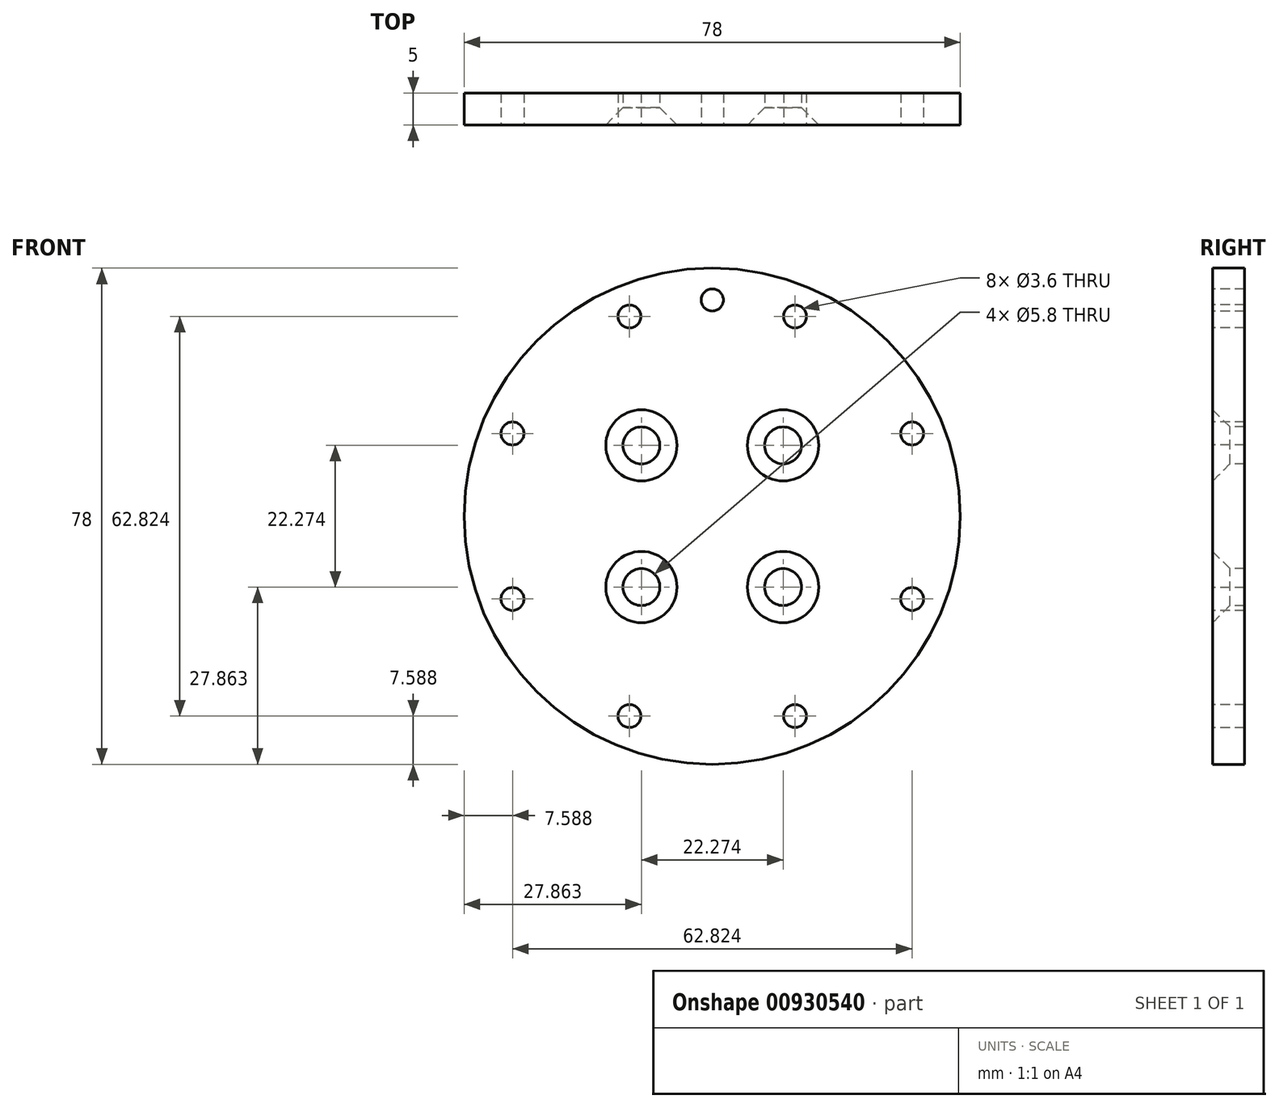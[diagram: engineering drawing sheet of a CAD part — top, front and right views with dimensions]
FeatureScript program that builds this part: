
annotation { "Feature Type Name" : "Feature", "Feature Type Description" : "" }
export const myFeature = defineFeature(function(context is Context, id is Id, definition is map)
    precondition{}
    {
        {
            var Q0;
            Q0=qCreatedBy(makeId("Front.planeOp"),FACE);
            var sketch = newSketch(context, id + "F0", { "sketchPlane" : qUnion([Q0])});
            skCircle(sketch, "E0", {"center": v(0, 0) * mm, "radius": 39 * mm});
            skSolve(sketch);
        }
        {
            var Q0;
            Q0 = qSketchRegion(id + "F0", true);
            extrude(context, id + "F1", {"entities" : qUnion([Q0]), "depth" : 5 * mm, "offsetDistance" : 25 * mm});
        }
        {
            var Q0;
            Q0=makeQuery(id+"F1.opExtrude","CAP_FACE",FACE,{"disambiguationData":[OSD([sQuery(id+"F0.wireOp",EDGE,"E0")])],"isStart":false});
            var sketch = newSketch(context, id + "F2", { "sketchPlane" : qUnion([Q0])});
            skCircle(sketch, "E1", {"center": v(0, 0) * mm, "radius": 34 * mm});
            skPoint(sketch, "E2", {"position": v(31.41, 13.01) * mm});
            skLineSegment(sketch, "E3", {"start": v(0, 0) * mm, "end": v(31.41, 13.01) * mm, "construction": true});
            skLineSegment(sketch, "E4", {"start": v(0, 0) * mm, "end": v(34, 0) * mm, "construction": true});
            skPoint(sketch, "E5.1.0", {"position": v(13.01, 31.41) * mm});
            skPoint(sketch, "E5.2.0", {"position": v(-13.01, 31.41) * mm});
            skPoint(sketch, "E5.3.0", {"position": v(-31.41, 13.01) * mm});
            skPoint(sketch, "E5.4.0", {"position": v(-31.41, -13.01) * mm});
            skPoint(sketch, "E5.5.0", {"position": v(-13.01, -31.41) * mm});
            skPoint(sketch, "E5.6.0", {"position": v(13.01, -31.41) * mm});
            skPoint(sketch, "E5.7.0", {"position": v(31.41, -13.01) * mm});
            skCircle(sketch, "E6", {"center": v(0, 34) * mm, "radius": 1.75 * mm});
            skSolve(sketch);
        }
        {
            var Q0;
            Q0=sQuery(id+"F2.wireOp",VERTEX,"E2");
            var Q1;
            Q1=sQuery(id+"F2.wireOp",VERTEX,"E5.1.0");
            var Q2;
            Q2=sQuery(id+"F2.wireOp",VERTEX,"E5.2.0");
            var Q3;
            Q3=sQuery(id+"F2.wireOp",VERTEX,"E5.3.0");
            var Q4;
            Q4=sQuery(id+"F2.wireOp",VERTEX,"E5.4.0");
            var Q5;
            Q5=sQuery(id+"F2.wireOp",VERTEX,"E5.5.0");
            var Q6;
            Q6=sQuery(id+"F2.wireOp",VERTEX,"E5.6.0");
            var Q7;
            Q7=sQuery(id+"F2.wireOp",VERTEX,"E5.7.0");
            var Q8;
            Q8=makeQuery(id+"F1.opExtrude","SWEPT_BODY",BODY,{"disambiguationData":[OSD([sQuery(id+"F0.wireOp",EDGE,"E0")])]});
            hole(context, id + "F3", {"style" : HoleStyle.SIMPLE, "endStyle" : HoleEndStyle.THROUGH, "standardTappedOrClearance" : lookupTablePath({ "fit" : "Loose", "standard" : "ISO", "size" : "M3", "type" : "Clearance" }), "standardBlindInLast" : lookupTablePath({ "fit" : "Loose", "standard" : "ISO", "engagement" : "75%", "pitch" : "0.5 mm", "size" : "M3", "type" : "Clearance & tapped" }), "holeDiameter" : 3.6 * mm, "majorDiameter" : 5 * mm, "isTappedThrough" : true, "tappedDepth" : 12 * mm, "tapClearance" : 3, "locations" : qUnion([Q0, Q1, Q2, Q3, Q4, Q5, Q6, Q7]), "scope" : qUnion([Q8])});
        }
        {
            var Q0;
            Q0=makeQuery(id+"F1.opExtrude","CAP_FACE",FACE,{"disambiguationData":[OSD([sQuery(id+"F0.wireOp",EDGE,"E0")])],"isStart":false});
            var sketch = newSketch(context, id + "F4", { "sketchPlane" : qUnion([Q0])});
            skCircle(sketch, "E7", {"center": v(0, 0) * mm, "radius": 15.75 * mm, "construction": true});
            skLineSegment(sketch, "E8", {"start": v(0, 0) * mm, "end": v(15.75, 0) * mm, "construction": true});
            skPoint(sketch, "E9", {"position": v(11.14, 11.14) * mm});
            skLineSegment(sketch, "E10", {"start": v(0, 0) * mm, "end": v(11.14, 11.14) * mm, "construction": true});
            skPoint(sketch, "E11.1.0", {"position": v(-11.14, 11.14) * mm});
            skPoint(sketch, "E11.2.0", {"position": v(-11.14, -11.14) * mm});
            skPoint(sketch, "E11.3.0", {"position": v(11.14, -11.14) * mm});
            skSolve(sketch);
        }
        {
            var Q0;
            Q0=sQuery(id+"F4.wireOp",VERTEX,"E9");
            var Q1;
            Q1=sQuery(id+"F4.wireOp",VERTEX,"E11.1.0");
            var Q2;
            Q2=sQuery(id+"F4.wireOp",VERTEX,"E11.2.0");
            var Q3;
            Q3=sQuery(id+"F4.wireOp",VERTEX,"E11.3.0");
            var Q4;
            Q4=makeQuery(id+"F1.opExtrude","SWEPT_BODY",BODY,{"disambiguationData":[OSD([sQuery(id+"F0.wireOp",EDGE,"E0")])]});
            hole(context, id + "F5", {"style" : HoleStyle.C_SINK, "endStyle" : HoleEndStyle.THROUGH, "standardTappedOrClearance" : lookupTablePath({ "fit" : "Loose", "standard" : "ISO", "size" : "M5", "type" : "Clearance" }), "standardBlindInLast" : lookupTablePath({ "fit" : "Loose", "standard" : "ISO", "engagement" : "75%", "pitch" : "0.8 mm", "size" : "M5", "type" : "Clearance & tapped" }), "holeDiameter" : 5.8 * mm, "cSinkDiameter" : 11.2 * mm, "cSinkAngle" : 90 * degree, "majorDiameter" : 5 * mm, "isTappedThrough" : true, "tappedDepth" : 12 * mm, "tapClearance" : 3, "locations" : qUnion([Q0, Q1, Q2, Q3]), "scope" : qUnion([Q4])});
        }
        {
            var Q0;
            {var subQ0=sQuery(id+"F2.wireOp",EDGE,"E6");var subQ1=sQuery(id+"F2.wireOp",EDGE,"E1");var subQ2=makeQuery(id+"F2.imprint","INTERSECT",VERTEX,{"disambiguationData":[OD(0.0)],"derivedFrom":[subQ1,subQ0]});Q0=makeQuery(id+"F2.imprint","IMPRINT",FACE,{"disambiguationData":[TD([[makeQuery(id+"F2.imprint","IMPRINT",EDGE,{"disambiguationData":[TD([[subQ2,1.0]])],"derivedFrom":subQ1}),1.0]])]});}
            var Q1;
            {var subQ0=sQuery(id+"F2.wireOp",EDGE,"E6");var subQ1=sQuery(id+"F2.wireOp",EDGE,"E1");var subQ2=makeQuery(id+"F2.imprint","INTERSECT",VERTEX,{"disambiguationData":[OD(0.0)],"derivedFrom":[subQ1,subQ0]});Q1=makeQuery(id+"F2.imprint","IMPRINT",FACE,{"disambiguationData":[TD([[makeQuery(id+"F2.imprint","IMPRINT",EDGE,{"disambiguationData":[TD([[subQ2,1.0]])],"derivedFrom":subQ1}),-1.0]])]});}
            extrude(context, id + "F6", {"entities" : qUnion([Q0, Q1]), "operationType" : NewBodyOperationType.REMOVE, "oppositeDirection" : true, "depth" : 25 * mm, "offsetDistance" : 25 * mm});
        }
    });
